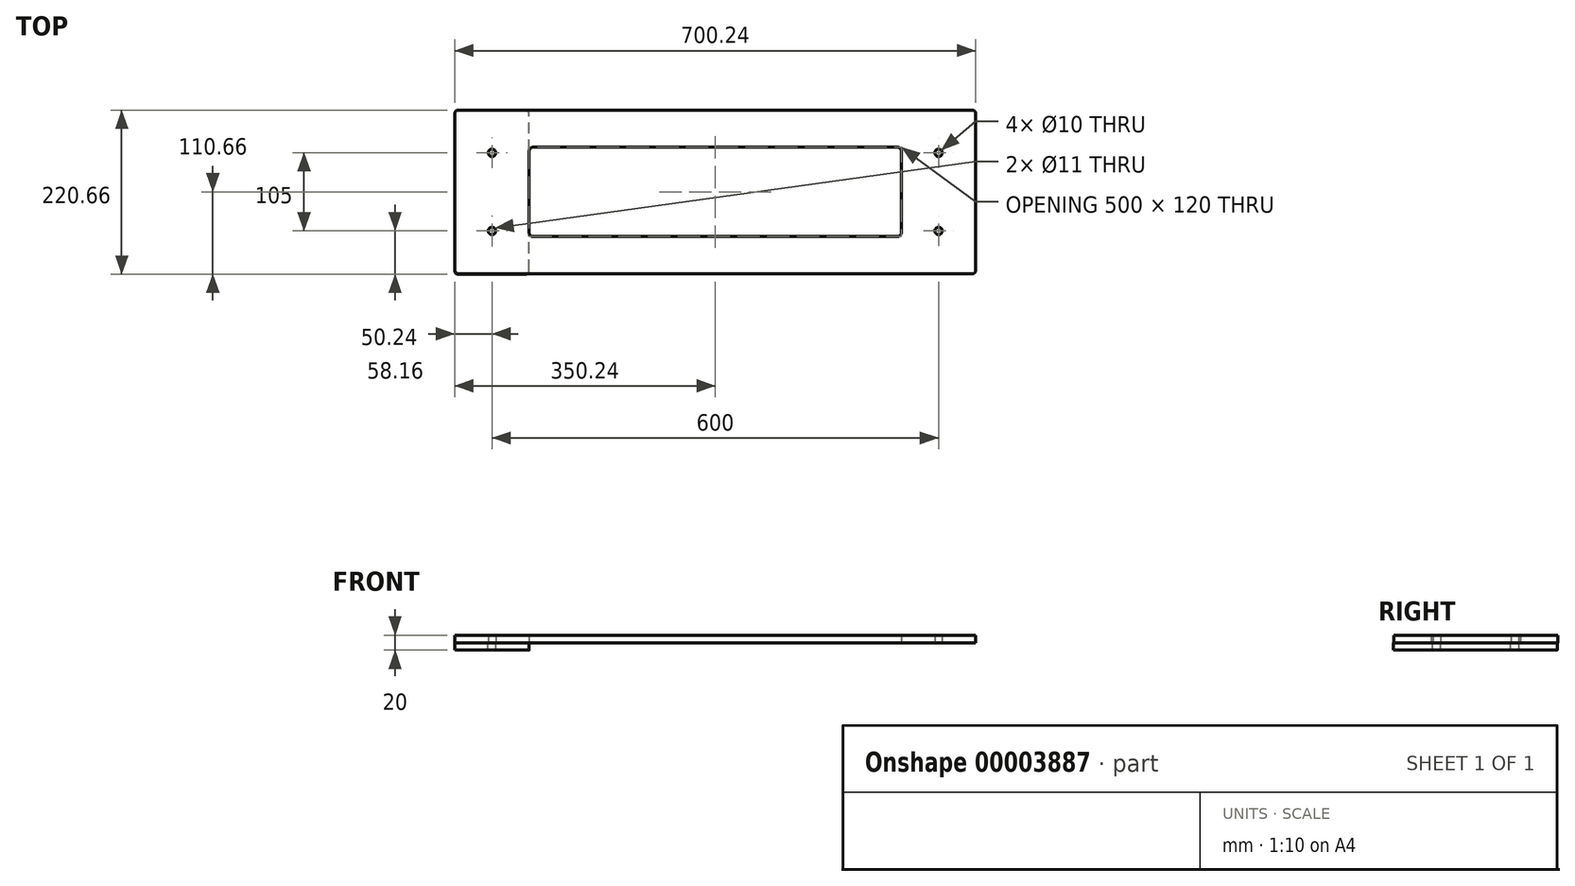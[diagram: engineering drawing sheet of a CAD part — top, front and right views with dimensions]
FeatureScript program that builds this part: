
annotation { "Feature Type Name" : "Feature", "Feature Type Description" : "" }
export const myFeature = defineFeature(function(context is Context, id is Id, definition is map)
    precondition{}
    {
        {
            var Q0;
            Q0=qCreatedBy(makeId("Top.planeOp"),FACE);
            var sketch = newSketch(context, id + "F0", { "sketchPlane" : qUnion([Q0])});
            skLineSegment(sketch, "E0.rect.bottom", {"start": v(-345, 110) * mm, "end": v(345, 110) * mm});
            skLineSegment(sketch, "E0.rect.top", {"start": v(-345, -110) * mm, "end": v(345, -110) * mm});
            skLineSegment(sketch, "E0.rect.left", {"start": v(-350, 105) * mm, "end": v(-350, -105) * mm});
            skLineSegment(sketch, "E0.rect.right", {"start": v(350, 105) * mm, "end": v(350, -105) * mm});
            skPoint(sketch, "E0.rect.middle", {"position": v(0, 0) * mm});
            skLineSegment(sketch, "E1.rect.bottom", {"start": v(-245, 60) * mm, "end": v(245, 60) * mm});
            skLineSegment(sketch, "E1.rect.top", {"start": v(-245, -60) * mm, "end": v(245, -60) * mm});
            skLineSegment(sketch, "E1.rect.left", {"start": v(-250, 55) * mm, "end": v(-250, -55) * mm});
            skLineSegment(sketch, "E1.rect.right", {"start": v(250, 55) * mm, "end": v(250, -55) * mm});
            skLineSegment(sketch, "E2.rect.bottom", {"start": v(-300, 52.5) * mm, "end": v(300, 52.5) * mm});
            skLineSegment(sketch, "E2.rect.top", {"start": v(-300, -52.5) * mm, "end": v(300, -52.5) * mm});
            skLineSegment(sketch, "E2.rect.left", {"start": v(-300, 52.5) * mm, "end": v(-300, -52.5) * mm});
            skLineSegment(sketch, "E2.rect.right", {"start": v(300, 52.5) * mm, "end": v(300, -52.5) * mm});
            skLineSegment(sketch, "E3", {"start": v(-250, 52.5) * mm, "end": v(-250, 60) * mm});
            skLineSegment(sketch, "E4", {"start": v(-250, 60) * mm, "end": v(-250, 110) * mm});
            skLineSegment(sketch, "E5", {"start": v(-250, -60) * mm, "end": v(-250, -110) * mm});
            skLineSegment(sketch, "E6", {"start": v(250, -60) * mm, "end": v(250, -110) * mm});
            skLineSegment(sketch, "E7", {"start": v(250, 60) * mm, "end": v(250, 110) * mm});
            skPoint(sketch, "E8.visualSharp", {"position": v(-250, 60) * mm});
            skArc(sketch, "E8.filletArc", {"start": v(-245, 60) * mm, "mid": v(-248.54, 58.54) * mm, "end": v(-250, 55) * mm});
            skPoint(sketch, "E9.visualSharp", {"position": v(-250, -60) * mm});
            skArc(sketch, "E9.filletArc", {"start": v(-250, -55) * mm, "mid": v(-248.54, -58.54) * mm, "end": v(-245, -60) * mm});
            skPoint(sketch, "E10.visualSharp", {"position": v(250, -60) * mm});
            skArc(sketch, "E10.filletArc", {"start": v(245, -60) * mm, "mid": v(248.54, -58.54) * mm, "end": v(250, -55) * mm});
            skPoint(sketch, "E11.visualSharp", {"position": v(250, 60) * mm});
            skArc(sketch, "E11.filletArc", {"start": v(250, 55) * mm, "mid": v(248.54, 58.54) * mm, "end": v(245, 60) * mm});
            skPoint(sketch, "E12.visualSharp", {"position": v(350, -110) * mm});
            skArc(sketch, "E12.filletArc", {"start": v(345, -110) * mm, "mid": v(348.54, -108.54) * mm, "end": v(350, -105) * mm});
            skPoint(sketch, "E13.visualSharp", {"position": v(350, 110) * mm});
            skArc(sketch, "E13.filletArc", {"start": v(350, 105) * mm, "mid": v(348.54, 108.54) * mm, "end": v(345, 110) * mm});
            skPoint(sketch, "E14.visualSharp", {"position": v(-350, 110) * mm});
            skArc(sketch, "E14.filletArc", {"start": v(-345, 110) * mm, "mid": v(-348.54, 108.54) * mm, "end": v(-350, 105) * mm});
            skPoint(sketch, "E15.visualSharp", {"position": v(-350, -110) * mm});
            skArc(sketch, "E15.filletArc", {"start": v(-350, -105) * mm, "mid": v(-348.54, -108.54) * mm, "end": v(-345, -110) * mm});
            skSolve(sketch);
        }
        {
            var Q0;
            Q0=makeQuery(id+"F0.imprint","IMPRINT",FACE,{"disambiguationData":[TD([[makeQuery(id+"F0.imprint","IMPRINT",EDGE,{"derivedFrom":sQuery(id+"F0.wireOp",EDGE,"E0.rect.left")}),1.0]])]});
            var Q1;
            Q1=makeQuery(id+"F0.imprint","IMPRINT",FACE,{"disambiguationData":[TD([[makeQuery(id+"F0.imprint","IMPRINT",EDGE,{"derivedFrom":sQuery(id+"F0.wireOp",EDGE,"E1.rect.bottom")}),1.0]])]});
            var Q2;
            {var subQ3=sQuery(id+"F0.wireOp",EDGE,"E0.rect.bottom");var subQ5=sQuery(id+"F0.wireOp",EDGE,"E4");var subQ7=makeQuery(id+"F0.imprint","INTERSECT",VERTEX,{"derivedFrom":[subQ3,subQ5]});Q2=makeQuery(id+"F0.imprint","IMPRINT",FACE,{"disambiguationData":[TD([[makeQuery(id+"F0.imprint","IMPRINT",EDGE,{"disambiguationData":[TD([[subQ7,-1.0]])],"derivedFrom":subQ3}),-1.0]])]});}
            var Q3;
            {var subQ3=sQuery(id+"F0.wireOp",EDGE,"E0.rect.top");var subQ5=sQuery(id+"F0.wireOp",EDGE,"E5");var subQ7=makeQuery(id+"F0.imprint","INTERSECT",VERTEX,{"derivedFrom":[subQ3,subQ5]});Q3=makeQuery(id+"F0.imprint","IMPRINT",FACE,{"disambiguationData":[TD([[makeQuery(id+"F0.imprint","IMPRINT",EDGE,{"disambiguationData":[TD([[subQ7,-1.0]])],"derivedFrom":subQ3}),1.0]])]});}
            var Q4;
            Q4=makeQuery(id+"F0.imprint","IMPRINT",FACE,{"disambiguationData":[TD([[makeQuery(id+"F0.imprint","IMPRINT",EDGE,{"derivedFrom":sQuery(id+"F0.wireOp",EDGE,"E0.rect.right")}),-1.0]])]});
            var Q5;
            {var subQ0=sQuery(id+"F0.wireOp",EDGE,"E2.rect.right");Q5=makeQuery(id+"F0.imprint","IMPRINT",FACE,{"disambiguationData":[TD([[makeQuery(id+"F0.imprint","IMPRINT",EDGE,{"derivedFrom":subQ0}),-1.0]])]});}
            var Q6;
            {var subQ0=sQuery(id+"F0.wireOp",EDGE,"E2.rect.left");Q6=makeQuery(id+"F0.imprint","IMPRINT",FACE,{"disambiguationData":[TD([[makeQuery(id+"F0.imprint","IMPRINT",EDGE,{"derivedFrom":subQ0}),1.0]])]});}
            extrude(context, id + "F1", {"entities" : qUnion([Q0, Q1, Q2, Q3, Q4, Q5, Q6]), "depth" : 10 * mm});
        }
        {
            var Q0;
            Q0=makeQuery(id+"F0.imprint","IMPRINT",FACE,{"disambiguationData":[TD([[makeQuery(id+"F0.imprint","IMPRINT",EDGE,{"derivedFrom":sQuery(id+"F0.wireOp",EDGE,"E1.rect.bottom")}),-1.0]])]});
            var sketch = newSketch(context, id + "F2", { "sketchPlane" : qUnion([Q0])});
            skLineSegment(sketch, "E16.bottom", {"start": v(-255.24, -110.66) * mm, "end": v(-345.24, -110.66) * mm});
            skLineSegment(sketch, "E16.top", {"start": v(-255.24, 109.34) * mm, "end": v(-345.24, 109.34) * mm});
            skLineSegment(sketch, "E16.left", {"start": v(-250.24, -105.66) * mm, "end": v(-250.24, 104.34) * mm});
            skLineSegment(sketch, "E16.right", {"start": v(-350.24, -105.66) * mm, "end": v(-350.24, 104.34) * mm});
            skPoint(sketch, "E17.visualSharp", {"position": v(-350.24, 109.34) * mm});
            skArc(sketch, "E17.filletArc", {"start": v(-345.24, 109.34) * mm, "mid": v(-348.77, 107.88) * mm, "end": v(-350.24, 104.34) * mm});
            skPoint(sketch, "E18.visualSharp", {"position": v(-250.24, 109.34) * mm});
            skArc(sketch, "E18.filletArc", {"start": v(-250.24, 104.34) * mm, "mid": v(-251.7, 107.88) * mm, "end": v(-255.24, 109.34) * mm});
            skPoint(sketch, "E19.visualSharp", {"position": v(-250.24, -110.66) * mm});
            skArc(sketch, "E19.filletArc", {"start": v(-255.24, -110.66) * mm, "mid": v(-251.7, -109.2) * mm, "end": v(-250.24, -105.66) * mm});
            skPoint(sketch, "E20.visualSharp", {"position": v(-350.24, -110.66) * mm});
            skArc(sketch, "E20.filletArc", {"start": v(-350.24, -105.66) * mm, "mid": v(-348.77, -109.2) * mm, "end": v(-345.24, -110.66) * mm});
            skSolve(sketch);
        }
        {
            var Q0;
            Q0 = qSketchRegion(id + "F2", true);
            extrude(context, id + "F3", {"entities" : qUnion([Q0]), "oppositeDirection" : true, "depth" : 10 * mm});
        }
        {
            var Q0;
            Q0=makeQuery(id+"F0.imprint","IMPRINT",FACE,{"disambiguationData":[TD([[makeQuery(id+"F0.imprint","IMPRINT",EDGE,{"derivedFrom":sQuery(id+"F0.wireOp",EDGE,"E1.rect.bottom")}),-1.0]])]});
            var sketch = newSketch(context, id + "F4", { "sketchPlane" : qUnion([Q0])});
            skCircle(sketch, "E21", {"center": v(-300, 52.5) * mm, "radius": 5 * mm});
            skCircle(sketch, "E22.0.1.0", {"center": v(-300, -52.5) * mm, "radius": 5 * mm});
            skCircle(sketch, "E22.1.0.0", {"center": v(300, 52.5) * mm, "radius": 5 * mm});
            skCircle(sketch, "E22.1.1.0", {"center": v(300, -52.5) * mm, "radius": 5 * mm});
            skLineSegment(sketch, "E22.direction1", {"start": v(-300, 52.5) * mm, "end": v(300, 52.5) * mm, "construction": true});
            skLineSegment(sketch, "E22.direction2", {"start": v(-300, 52.5) * mm, "end": v(-300, -52.5) * mm, "construction": true});
            skSolve(sketch);
        }
        {
            var Q0;
            Q0 = qSketchRegion(id + "F4", true);
            extrude(context, id + "F5", {"entities" : qUnion([Q0]), "operationType" : NewBodyOperationType.REMOVE, "depth" : 25 * mm});
        }
        {
            var Q0;
            {var subQ3=sQuery(id+"F0.wireOp",EDGE,"E0.rect.top");var subQ5=sQuery(id+"F0.wireOp",EDGE,"E5");var subQ7=makeQuery(id+"F0.imprint","INTERSECT",VERTEX,{"derivedFrom":[subQ3,subQ5]});Q0=makeQuery(id+"F0.imprint","IMPRINT",FACE,{"disambiguationData":[TD([[makeQuery(id+"F0.imprint","IMPRINT",EDGE,{"disambiguationData":[TD([[subQ7,-1.0]])],"derivedFrom":subQ3}),1.0]])]});}
            var sketch = newSketch(context, id + "F6", { "sketchPlane" : qUnion([Q0])});
            skCircle(sketch, "E23", {"center": v(-300, -52.5) * mm, "radius": 5.5 * mm});
            skCircle(sketch, "E24", {"center": v(-300, 52.5) * mm, "radius": 5.5 * mm});
            skSolve(sketch);
        }
        {
            var Q0;
            Q0 = qSketchRegion(id + "F6", true);
            extrude(context, id + "F7", {"entities" : qUnion([Q0]), "operationType" : NewBodyOperationType.REMOVE, "oppositeDirection" : true, "depth" : 25 * mm});
        }
    });
